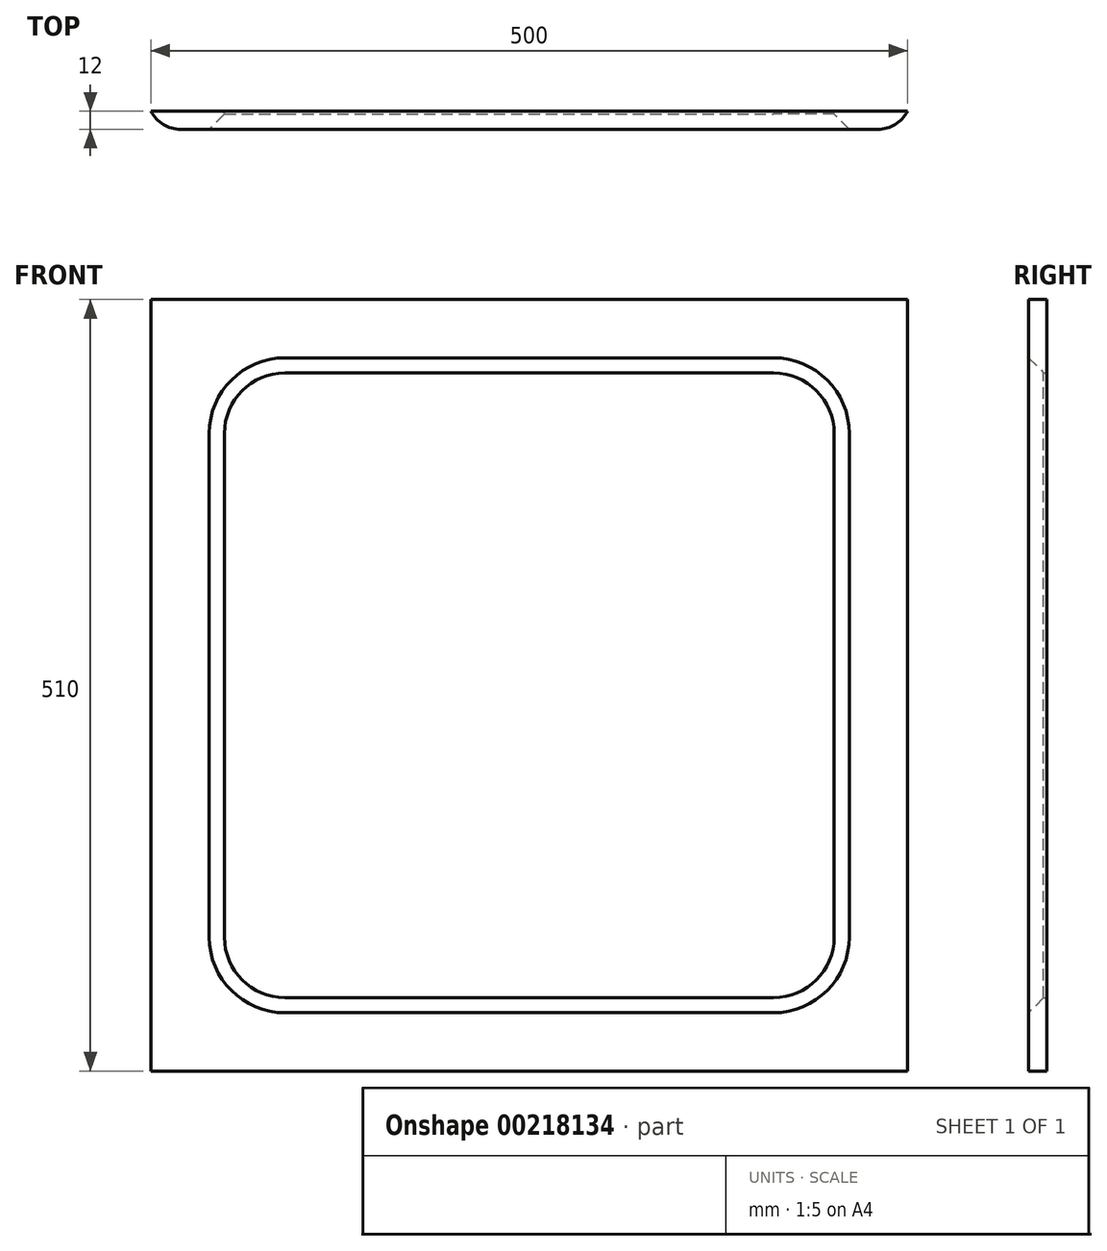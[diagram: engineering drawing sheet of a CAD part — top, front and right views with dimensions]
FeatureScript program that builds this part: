
annotation { "Feature Type Name" : "Feature", "Feature Type Description" : "" }
export const myFeature = defineFeature(function(context is Context, id is Id, definition is map)
    precondition{}
    {
        {
            var Q0;
            Q0=qCreatedBy(makeId("Front.planeOp"),FACE);
            var sketch = newSketch(context, id + "F0", { "sketchPlane" : qUnion([Q0])});
            skLineSegment(sketch, "E0.bottom", {"start": v(251.52, 255) * mm, "end": v(-248.48, 255) * mm});
            skLineSegment(sketch, "E0.top", {"start": v(251.52, -255) * mm, "end": v(-248.48, -255) * mm});
            skLineSegment(sketch, "E0.left", {"start": v(251.52, 255) * mm, "end": v(251.52, -255) * mm});
            skLineSegment(sketch, "E0.right", {"start": v(-248.48, 255) * mm, "end": v(-248.48, -255) * mm});
            skPoint(sketch, "E0.middle", {"position": v(1.52, 0) * mm});
            skPoint(sketch, "E1.middle", {"position": v(0, 0) * mm});
            skLineSegment(sketch, "E2.bottom", {"start": v(-159.98, 206.5) * mm, "end": v(163.02, 206.5) * mm});
            skLineSegment(sketch, "E2.top", {"start": v(-159.98, -206.5) * mm, "end": v(163.02, -206.5) * mm});
            skLineSegment(sketch, "E2.left", {"start": v(-199.98, 166.5) * mm, "end": v(-199.98, -166.5) * mm});
            skLineSegment(sketch, "E2.right", {"start": v(203.02, 166.5) * mm, "end": v(203.02, -166.5) * mm});
            skPoint(sketch, "E3.visualSharp", {"position": v(-199.98, 206.5) * mm});
            skArc(sketch, "E3.filletArc", {"start": v(-159.98, 206.5) * mm, "mid": v(-188.26, 194.78) * mm, "end": v(-199.98, 166.5) * mm});
            skPoint(sketch, "E4.visualSharp", {"position": v(203.02, 206.5) * mm});
            skArc(sketch, "E4.filletArc", {"start": v(203.02, 166.5) * mm, "mid": v(191.3, 194.78) * mm, "end": v(163.02, 206.5) * mm});
            skPoint(sketch, "E5.visualSharp", {"position": v(203.02, -206.5) * mm});
            skArc(sketch, "E5.filletArc", {"start": v(163.02, -206.5) * mm, "mid": v(191.3, -194.78) * mm, "end": v(203.02, -166.5) * mm});
            skPoint(sketch, "E6.visualSharp", {"position": v(-199.98, -206.5) * mm});
            skArc(sketch, "E6.filletArc", {"start": v(-199.98, -166.5) * mm, "mid": v(-188.26, -194.78) * mm, "end": v(-159.98, -206.5) * mm});
            skCircle(sketch, "E7", {"center": v(1.52, -5) * mm, "radius": 177.5 * mm});
            skSolve(sketch);
        }
        {
            var Q0;
            Q0=makeQuery(id+"F0.imprint","IMPRINT",FACE,{"disambiguationData":[TD([[makeQuery(id+"F0.imprint","IMPRINT",EDGE,{"derivedFrom":sQuery(id+"F0.wireOp",EDGE,"E0.bottom")}),1.0]])]});
            extrude(context, id + "F1", {"entities" : qUnion([Q0]), "depth" : 12 * mm});
        }
        {
            var Q0;
            Q0=makeQuery(id+"F1.opExtrude","CAP_EDGE",EDGE,{"disambiguationData":[OSD([sQuery(id+"F0.wireOp",EDGE,"E2.bottom")])],"isStart":false});
            chamfer(context, id + "F2", {"entities" : qUnion([Q0]), "width" : 10 * mm, "tangentPropagation" : true});
        }
        {
            var Q0;
            Q0=makeQuery(id+"F1.opExtrude","CAP_EDGE",EDGE,{"disambiguationData":[OSD([sQuery(id+"F0.wireOp",EDGE,"E0.right")])],"isStart":false});
            var Q1;
            Q1=makeQuery(id+"F1.opExtrude","CAP_EDGE",EDGE,{"disambiguationData":[OSD([sQuery(id+"F0.wireOp",EDGE,"E0.left")])],"isStart":false});
            fillet(context, id + "F3", {"entities" : qUnion([Q0, Q1]), "radius" : 22 * mm, "tangentPropagation" : true, "allowEdgeOverflow" : false});
        }
    });
